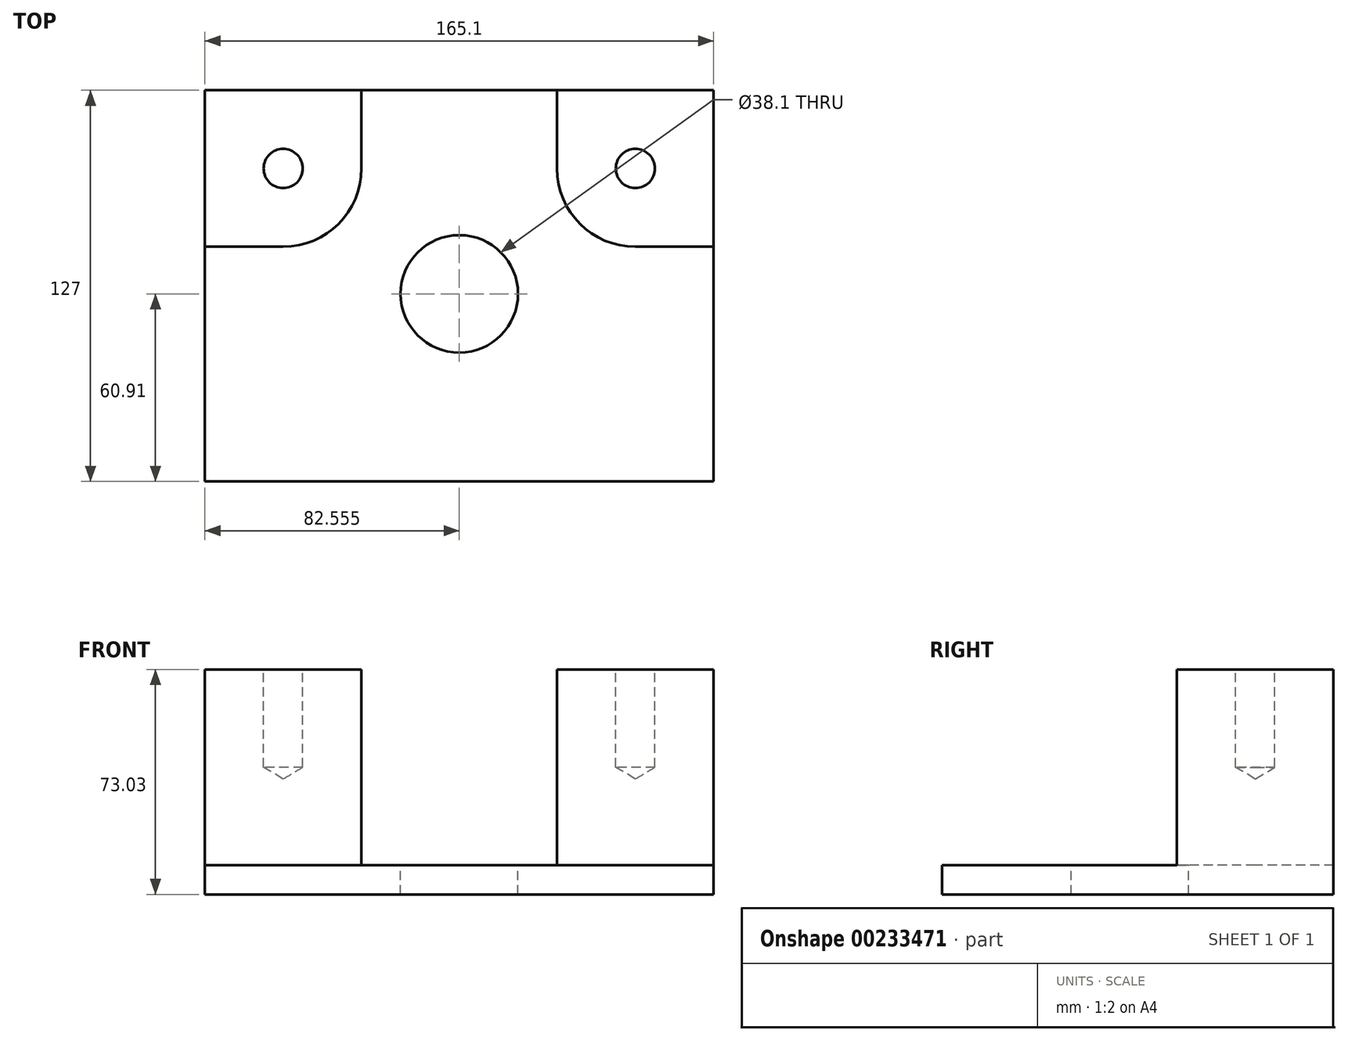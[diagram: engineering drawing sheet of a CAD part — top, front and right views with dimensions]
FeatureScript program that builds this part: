
annotation { "Feature Type Name" : "Feature", "Feature Type Description" : "" }
export const myFeature = defineFeature(function(context is Context, id is Id, definition is map)
    precondition{}
    {
        {
            var Q0;
            Q0=qCreatedBy(makeId("Top.planeOp"),FACE);
            var sketch = newSketch(context, id + "F0", { "sketchPlane" : qUnion([Q0])});
            skLineSegment(sketch, "E0.bottom", {"start": v(-88.53, 66.1) * mm, "end": v(76.57, 66.1) * mm});
            skLineSegment(sketch, "E0.top", {"start": v(-88.53, -60.9) * mm, "end": v(76.57, -60.9) * mm});
            skLineSegment(sketch, "E0.left", {"start": v(-88.53, 66.1) * mm, "end": v(-88.53, -60.9) * mm});
            skLineSegment(sketch, "E0.right", {"start": v(76.57, 66.1) * mm, "end": v(76.57, -60.9) * mm});
            skSolve(sketch);
        }
        {
            var Q0;
            Q0 = qSketchRegion(id + "F0", true);
            extrude(context, id + "F1", {"entities" : qUnion([Q0]), "depth" : 9.52 * mm});
        }
        {
            var Q0;
            Q0=makeQuery(id+"F1.opExtrude","CAP_FACE",FACE,{"disambiguationData":[OSD([sQuery(id+"F0.wireOp",EDGE,"E0.bottom"),sQuery(id+"F0.wireOp",EDGE,"E0.top"),sQuery(id+"F0.wireOp",EDGE,"E0.left"),sQuery(id+"F0.wireOp",EDGE,"E0.right")])],"isStart":false});
            var sketch = newSketch(context, id + "F2", { "sketchPlane" : qUnion([Q0])});
            skLineSegment(sketch, "E1.bottom", {"start": v(-88.53, 66.1) * mm, "end": v(-37.73, 66.1) * mm});
            skLineSegment(sketch, "E1.top", {"start": v(-88.53, 15.3) * mm, "end": v(-63.13, 15.3) * mm});
            skLineSegment(sketch, "E1.left", {"start": v(-88.53, 66.1) * mm, "end": v(-88.53, 15.3) * mm});
            skLineSegment(sketch, "E1.right", {"start": v(-37.73, 66.1) * mm, "end": v(-37.73, 40.7) * mm});
            skLineSegment(sketch, "E2.bottom", {"start": v(76.57, 66.1) * mm, "end": v(25.77, 66.1) * mm});
            skLineSegment(sketch, "E2.top", {"start": v(76.57, 15.3) * mm, "end": v(51.17, 15.3) * mm});
            skLineSegment(sketch, "E2.left", {"start": v(76.57, 66.1) * mm, "end": v(76.57, 15.3) * mm});
            skLineSegment(sketch, "E2.right", {"start": v(25.77, 66.1) * mm, "end": v(25.77, 40.7) * mm});
            skPoint(sketch, "E3.visualSharp", {"position": v(-37.73, 15.3) * mm});
            skArc(sketch, "E3.filletArc", {"start": v(-63.13, 15.3) * mm, "mid": v(-45.16, 22.73) * mm, "end": v(-37.73, 40.7) * mm});
            skPoint(sketch, "E4.visualSharp", {"position": v(25.77, 15.3) * mm});
            skArc(sketch, "E4.filletArc", {"start": v(25.77, 40.7) * mm, "mid": v(33.21, 22.73) * mm, "end": v(51.17, 15.3) * mm});
            skSolve(sketch);
        }
        {
            var Q0;
            Q0=makeQuery(id+"F2.imprint","IMPRINT",FACE,{"disambiguationData":[TD([[makeQuery(id+"F2.imprint","IMPRINT",EDGE,{"derivedFrom":sQuery(id+"F2.wireOp",EDGE,"E1.bottom")}),-1.0]])]});
            var Q1;
            Q1=makeQuery(id+"F2.imprint","IMPRINT",FACE,{"disambiguationData":[TD([[makeQuery(id+"F2.imprint","IMPRINT",EDGE,{"derivedFrom":sQuery(id+"F2.wireOp",EDGE,"E2.bottom")}),-1.0]])]});
            extrude(context, id + "F3", {"entities" : qUnion([Q0, Q1]), "operationType" : NewBodyOperationType.ADD, "depth" : 63.5 * mm});
        }
        {
            var Q0;
            Q0=makeQuery(id+"F3.opExtrude","CAP_FACE",FACE,{"disambiguationData":[OSD([sQuery(id+"F2.wireOp",EDGE,"E1.bottom"),sQuery(id+"F2.wireOp",EDGE,"E1.top"),sQuery(id+"F2.wireOp",EDGE,"E1.left"),sQuery(id+"F2.wireOp",EDGE,"E1.right"),sQuery(id+"F2.wireOp",EDGE,"E3.filletArc")])],"isStart":false});
            var sketch = newSketch(context, id + "F4", { "sketchPlane" : qUnion([Q0])});
            skCircle(sketch, "E5", {"center": v(-63.13, 40.7) * mm, "radius": 7.8 * mm});
            skSolve(sketch);
        }
        {
            var Q0;
            Q0=sQuery(id+"F4.wireOp",VERTEX,"E5.center");
            var Q1;
            Q1=makeQuery(id+"F1.opExtrude","SWEPT_BODY",BODY,{"disambiguationData":[OSD([sQuery(id+"F0.wireOp",EDGE,"E0.bottom"),sQuery(id+"F0.wireOp",EDGE,"E0.top"),sQuery(id+"F0.wireOp",EDGE,"E0.left"),sQuery(id+"F0.wireOp",EDGE,"E0.right")])]});
            hole(context, id + "F5", {"style" : HoleStyle.SIMPLE, "endStyle" : HoleEndStyle.BLIND, "holeDiameter" : 12.7 * mm, "holeDepth" : 31.75 * mm, "locations" : qUnion([Q0]), "scope" : qUnion([Q1])});
        }
        {
            var Q0;
            Q0=makeQuery(id+"F3.opExtrude","CAP_FACE",FACE,{"disambiguationData":[OSD([sQuery(id+"F2.wireOp",EDGE,"E2.bottom"),sQuery(id+"F2.wireOp",EDGE,"E2.top"),sQuery(id+"F2.wireOp",EDGE,"E2.left"),sQuery(id+"F2.wireOp",EDGE,"E2.right"),sQuery(id+"F2.wireOp",EDGE,"E4.filletArc")])],"isStart":false});
            var sketch = newSketch(context, id + "F6", { "sketchPlane" : qUnion([Q0])});
            skCircle(sketch, "E6", {"center": v(51.17, 40.7) * mm, "radius": 9.74 * mm});
            skSolve(sketch);
        }
        {
            var Q0;
            Q0=sQuery(id+"F6.wireOp",VERTEX,"E6.center");
            var Q1;
            Q1=makeQuery(id+"F1.opExtrude","SWEPT_BODY",BODY,{"disambiguationData":[OSD([sQuery(id+"F0.wireOp",EDGE,"E0.bottom"),sQuery(id+"F0.wireOp",EDGE,"E0.top"),sQuery(id+"F0.wireOp",EDGE,"E0.left"),sQuery(id+"F0.wireOp",EDGE,"E0.right")])]});
            hole(context, id + "F7", {"style" : HoleStyle.SIMPLE, "endStyle" : HoleEndStyle.BLIND, "holeDiameter" : 12.7 * mm, "holeDepth" : 31.75 * mm, "locations" : qUnion([Q0]), "scope" : qUnion([Q1])});
        }
        {
            var Q0;
            Q0=makeQuery(id+"F1.opExtrude","CAP_FACE",FACE,{"disambiguationData":[OSD([sQuery(id+"F0.wireOp",EDGE,"E0.bottom"),sQuery(id+"F0.wireOp",EDGE,"E0.top"),sQuery(id+"F0.wireOp",EDGE,"E0.left"),sQuery(id+"F0.wireOp",EDGE,"E0.right")])],"isStart":false});
            var sketch = newSketch(context, id + "F8", { "sketchPlane" : qUnion([Q0])});
            skCircle(sketch, "E7", {"center": v(-5.98, 0) * mm, "radius": 17.82 * mm});
            skPoint(sketch, "E8.trimOffspring.end.orphan", {"position": v(76.57, 0) * mm});
            skPoint(sketch, "E9.trimOffspring.end.orphan", {"position": v(-5.98, -60.9) * mm});
            skPoint(sketch, "E10.start.orphan", {"position": v(-88.53, 0) * mm});
            skPoint(sketch, "E11.start.orphan", {"position": v(-5.98, 66.1) * mm});
            skSolve(sketch);
        }
        {
            var Q0;
            Q0=sQuery(id+"F8.wireOp",VERTEX,"E7.center");
            var Q1;
            Q1=makeQuery(id+"F1.opExtrude","SWEPT_BODY",BODY,{"disambiguationData":[OSD([sQuery(id+"F0.wireOp",EDGE,"E0.bottom"),sQuery(id+"F0.wireOp",EDGE,"E0.top"),sQuery(id+"F0.wireOp",EDGE,"E0.left"),sQuery(id+"F0.wireOp",EDGE,"E0.right")])]});
            hole(context, id + "F9", {"style" : HoleStyle.SIMPLE, "endStyle" : HoleEndStyle.THROUGH, "holeDiameter" : 38.1 * mm, "locations" : qUnion([Q0]), "scope" : qUnion([Q1]), "isTappedThrough" : true});
        }
    });
